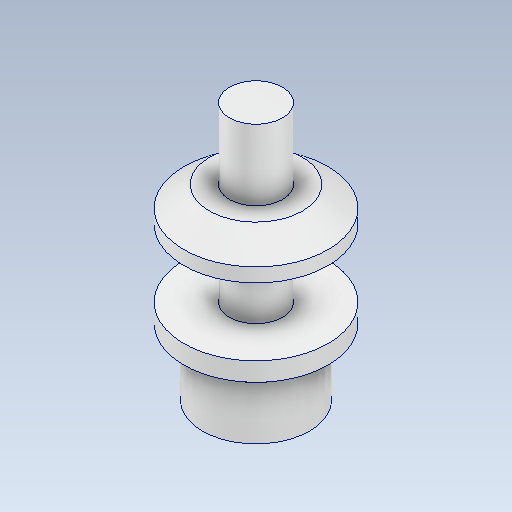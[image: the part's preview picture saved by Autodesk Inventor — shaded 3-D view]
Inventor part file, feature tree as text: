
AUTODESK INVENTOR PART (.ipt)
format: ipt  version: 2023 (Build 270158000, 158)  size: 156,160 bytes
history: native  units: in
note: dims shown in document units (in); Inventor stores cm internally (conversion verified against a paired STEP export)
features: revolve x1, sketch x1
ambient origin geometry x8: Origin, YZ Plane, XZ Plane, XY Plane, X Axis, Y Axis, Z Axis, Center Point
bodies: Solid1 (feature_tree)
feature tree (2):
  revolve  "Revolution1"  [1 undecoded]
  sketch  "Sketch1"  dims[d0=0.1476in d1=0.1378in d2=0.0591in d3=0.1102in d4=0.3937in d5=0.1378in d6=0.0984in d7=0.1378in d8=0.1969in d9=0.5in d10=0.1024in d11=0.1535in d12=0.189in d13=1.9685in d14=90.0deg]
note: 1 required parameter value undecoded (feature->parameter linkage not recoverable at this tier; creation-order binding heuristic only, values carry confidence <= 0.55)
